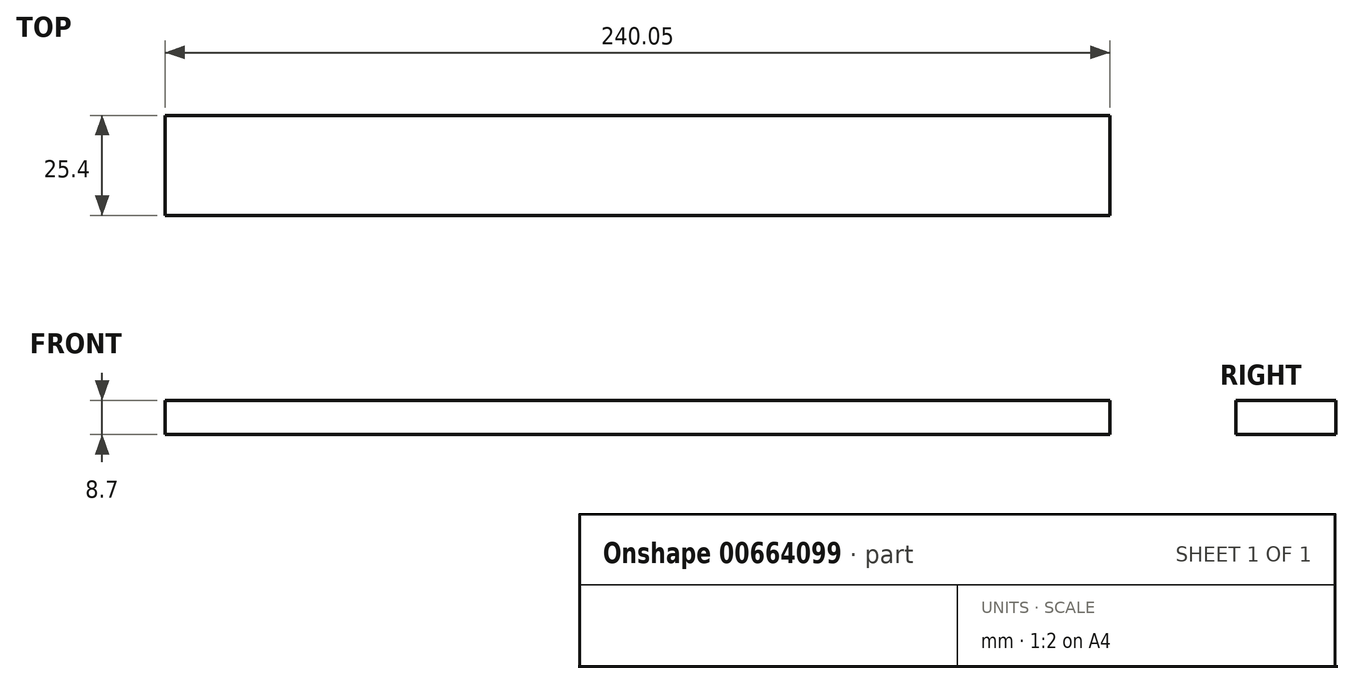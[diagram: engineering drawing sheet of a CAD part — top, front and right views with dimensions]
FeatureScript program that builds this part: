
annotation { "Feature Type Name" : "Feature", "Feature Type Description" : "" }
export const myFeature = defineFeature(function(context is Context, id is Id, definition is map)
    precondition{}
    {
        {
            var Q0;
            Q0=qCreatedBy(makeId("Front.planeOp"),FACE);
            var sketch = newSketch(context, id + "F0", { "sketchPlane" : qUnion([Q0])});
            skLineSegment(sketch, "E0.bottom", {"start": v(-124.93, 16.16) * mm, "end": v(115.12, 16.16) * mm});
            skLineSegment(sketch, "E0.top", {"start": v(-124.93, 24.86) * mm, "end": v(115.12, 24.86) * mm});
            skLineSegment(sketch, "E0.left", {"start": v(-124.93, 16.16) * mm, "end": v(-124.93, 24.86) * mm});
            skLineSegment(sketch, "E0.right", {"start": v(115.12, 16.16) * mm, "end": v(115.12, 24.86) * mm});
            skSolve(sketch);
        }
        {
            var Q0;
            Q0 = qSketchRegion(id + "F0", true);
            extrude(context, id + "F1", {"entities" : qUnion([Q0]), "depth" : 25.4 * mm, "offsetDistance" : 25.4 * mm});
        }
    });
